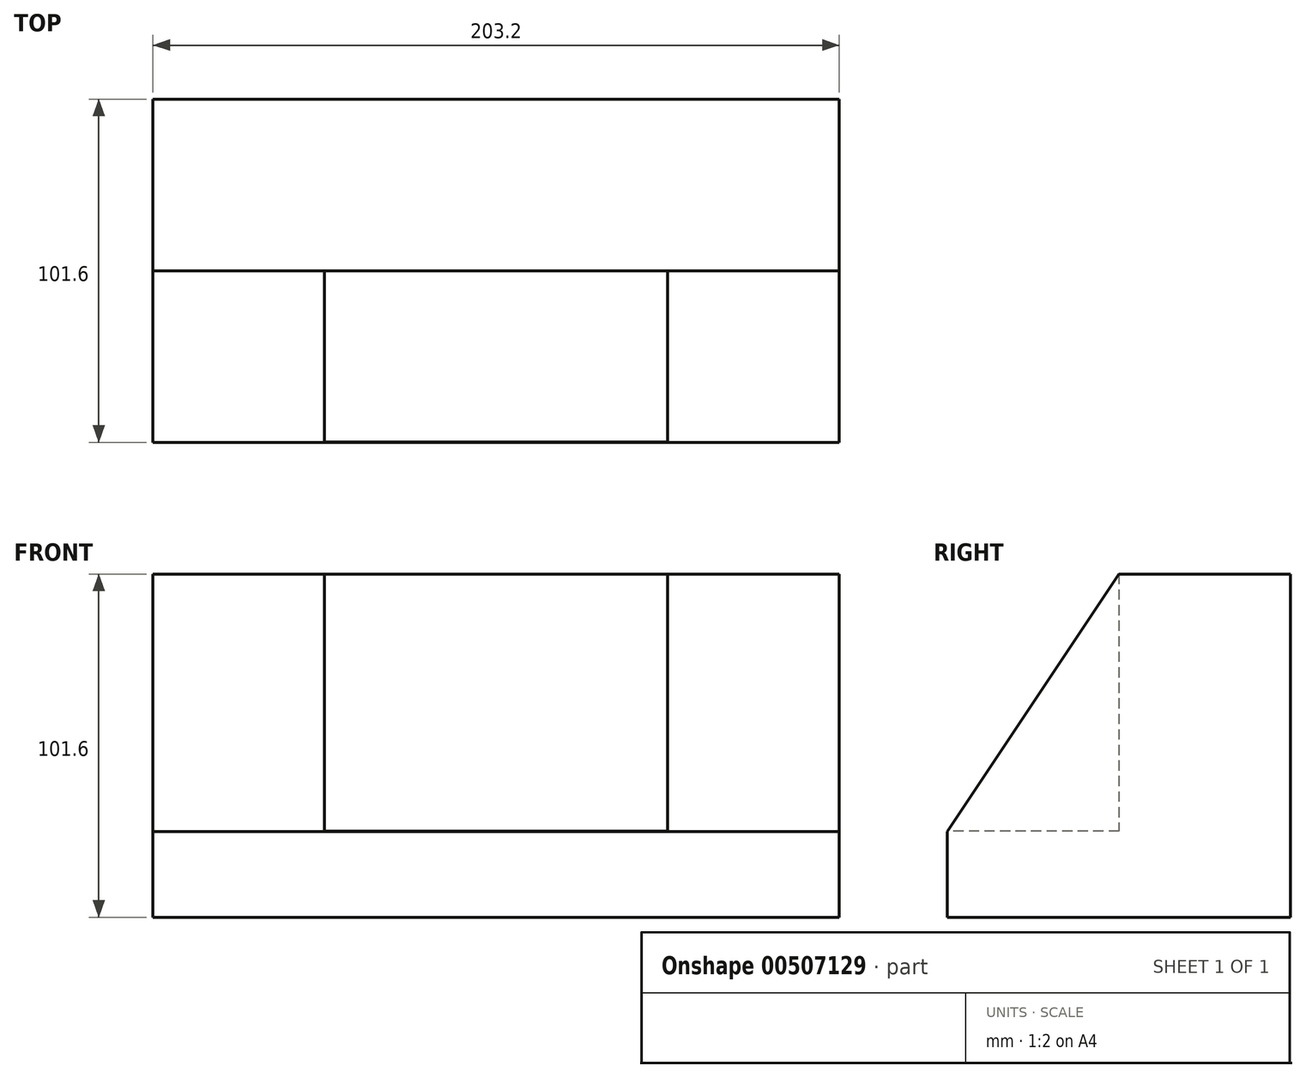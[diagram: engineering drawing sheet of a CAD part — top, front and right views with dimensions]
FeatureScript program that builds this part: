
annotation { "Feature Type Name" : "Feature", "Feature Type Description" : "" }
export const myFeature = defineFeature(function(context is Context, id is Id, definition is map)
    precondition{}
    {
        {
            var Q0;
            Q0=qCreatedBy(makeId("Front.planeOp"),FACE);
            var sketch = newSketch(context, id + "F0", { "sketchPlane" : qUnion([Q0])});
            skLineSegment(sketch, "E0.bottom", {"start": v(-98.33, 10.98) * mm, "end": v(104.87, 10.98) * mm});
            skLineSegment(sketch, "E0.top", {"start": v(-98.33, -90.62) * mm, "end": v(104.87, -90.62) * mm});
            skLineSegment(sketch, "E0.left", {"start": v(-98.33, 10.98) * mm, "end": v(-98.33, -90.62) * mm});
            skLineSegment(sketch, "E0.right", {"start": v(104.87, 10.98) * mm, "end": v(104.87, -90.62) * mm});
            skSolve(sketch);
        }
        {
            var Q0;
            Q0 = qSketchRegion(id + "F0", true);
            extrude(context, id + "F1", {"entities" : qUnion([Q0]), "oppositeDirection" : true, "depth" : 101.6 * mm});
        }
        {
            var Q0;
            Q0=makeQuery(id+"F1.opExtrude","CAP_EDGE",EDGE,{"disambiguationData":[OSD([sQuery(id+"F0.wireOp",EDGE,"E0.bottom")])],"isStart":true});
            chamfer(context, id + "F2", {"entities" : qUnion([Q0]), "chamferType" : ChamferType.TWO_OFFSETS, "width1" : 50.8 * mm, "oppositeDirection" : false, "width2" : 76.2 * mm, "tangentPropagation" : true});
        }
        {
            var Q0;
            Q0=qCreatedBy(makeId("Front.planeOp"),FACE);
            var sketch = newSketch(context, id + "F3", { "sketchPlane" : qUnion([Q0])});
            skLineSegment(sketch, "E1.bottom", {"start": v(-47.53, 11.08) * mm, "end": v(54.07, 11.08) * mm});
            skLineSegment(sketch, "E1.top", {"start": v(-47.53, -65.12) * mm, "end": v(54.07, -65.12) * mm});
            skLineSegment(sketch, "E1.left", {"start": v(-47.53, 11.08) * mm, "end": v(-47.53, -65.12) * mm});
            skLineSegment(sketch, "E1.right", {"start": v(54.07, 11.08) * mm, "end": v(54.07, -65.12) * mm});
            skSolve(sketch);
        }
        {
            var Q0;
            Q0 = qSketchRegion(id + "F3", true);
            extrude(context, id + "F4", {"entities" : qUnion([Q0]), "operationType" : NewBodyOperationType.REMOVE, "oppositeDirection" : true, "depth" : 50.8 * mm});
        }
    });
